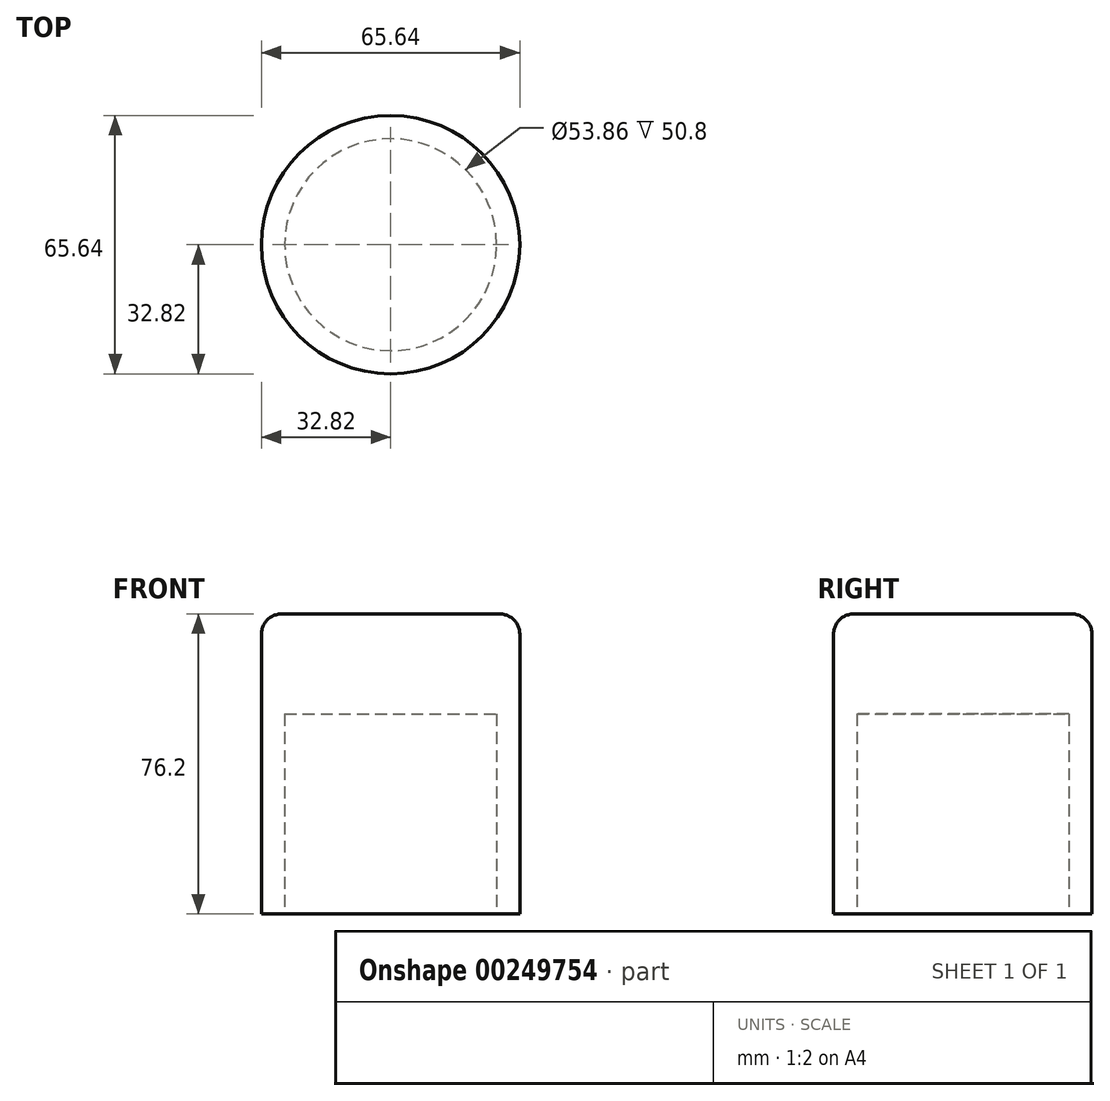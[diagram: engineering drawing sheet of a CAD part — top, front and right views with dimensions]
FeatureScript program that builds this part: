
annotation { "Feature Type Name" : "Feature", "Feature Type Description" : "" }
export const myFeature = defineFeature(function(context is Context, id is Id, definition is map)
    precondition{}
    {
        {
            var Q0;
            Q0=qCreatedBy(makeId("Top.planeOp"),FACE);
            var sketch = newSketch(context, id + "F0", { "sketchPlane" : qUnion([Q0])});
            skCircle(sketch, "E0", {"center": v(0, 0) * mm, "radius": 32.82 * mm});
            skSolve(sketch);
        }
        {
            var Q0;
            Q0=makeQuery(id+"F0.imprint","IMPRINT",FACE,{"disambiguationData":[TD([[makeQuery(id+"F0.imprint","IMPRINT",EDGE,{"derivedFrom":sQuery(id+"F0.wireOp",EDGE,"E0")}),1.0]])]});
            extrude(context, id + "F1", {"entities" : qUnion([Q0]), "depth" : 76.2 * mm});
        }
        {
            var Q0;
            Q0=makeQuery(id+"F1.opExtrude","CAP_FACE",FACE,{"disambiguationData":[OSD([sQuery(id+"F0.wireOp",EDGE,"E0")])],"isStart":false});
            fillet(context, id + "F2", {"entities" : qUnion([Q0]), "radius" : 5.08 * mm, "tangentPropagation" : true, "allowEdgeOverflow" : false});
        }
        {
            var Q0;
            Q0=makeQuery(id+"F1.opExtrude","CAP_FACE",FACE,{"disambiguationData":[OSD([sQuery(id+"F0.wireOp",EDGE,"E0")])],"isStart":true});
            var sketch = newSketch(context, id + "F3", { "sketchPlane" : qUnion([Q0])});
            skCircle(sketch, "E1", {"center": v(0, 0) * mm, "radius": 26.93 * mm});
            skSolve(sketch);
        }
        {
            var Q0;
            Q0=makeQuery(id+"F3.imprint","IMPRINT",FACE,{"disambiguationData":[TD([[makeQuery(id+"F3.imprint","IMPRINT",EDGE,{"derivedFrom":sQuery(id+"F3.wireOp",EDGE,"E1")}),1.0]])]});
            extrude(context, id + "F4", {"entities" : qUnion([Q0]), "operationType" : NewBodyOperationType.REMOVE, "oppositeDirection" : true, "depth" : 50.8 * mm});
        }
    });
